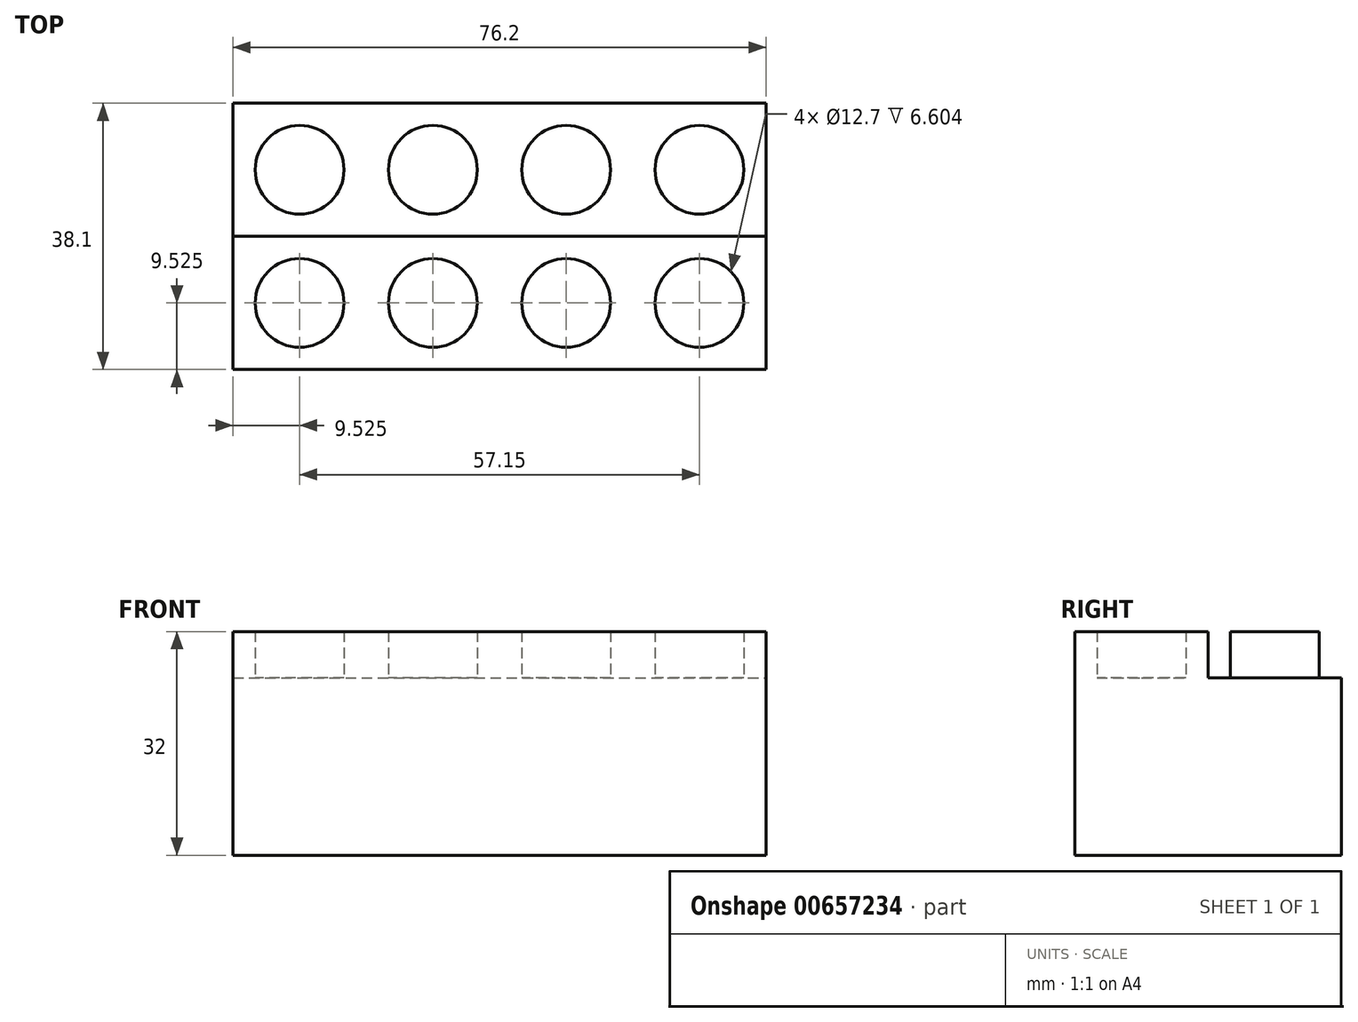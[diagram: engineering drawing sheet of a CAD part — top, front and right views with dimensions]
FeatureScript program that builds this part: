
annotation { "Feature Type Name" : "Feature", "Feature Type Description" : "" }
export const myFeature = defineFeature(function(context is Context, id is Id, definition is map)
    precondition{}
    {
        {
            var Q0;
            Q0=qCreatedBy(makeId("Top.planeOp"),FACE);
            var sketch = newSketch(context, id + "F0", { "sketchPlane" : qUnion([Q0])});
            skLineSegment(sketch, "E0.bottom", {"start": v(0, 0) * mm, "end": v(-76.2, 0) * mm});
            skLineSegment(sketch, "E0.top", {"start": v(0, 38.1) * mm, "end": v(-76.2, 38.1) * mm});
            skLineSegment(sketch, "E0.left", {"start": v(0, 0) * mm, "end": v(0, 38.1) * mm});
            skLineSegment(sketch, "E0.right", {"start": v(-76.2, 0) * mm, "end": v(-76.2, 38.1) * mm});
            skSolve(sketch);
        }
        {
            var Q0;
            Q0=makeQuery(id+"F0.imprint","IMPRINT",FACE,{"disambiguationData":[TD([[makeQuery(id+"F0.imprint","IMPRINT",EDGE,{"derivedFrom":sQuery(id+"F0.wireOp",EDGE,"E0.bottom")}),-1.0]])]});
            extrude(context, id + "F1", {"entities" : qUnion([Q0]), "depth" : 25.4 * mm, "offsetDistance" : 25.4 * mm});
        }
        {
            var Q0;
            Q0=makeQuery(id+"F1.opExtrude","CAP_FACE",FACE,{"disambiguationData":[OSD([sQuery(id+"F0.wireOp",EDGE,"E0.bottom"),sQuery(id+"F0.wireOp",EDGE,"E0.top"),sQuery(id+"F0.wireOp",EDGE,"E0.left"),sQuery(id+"F0.wireOp",EDGE,"E0.right")])],"isStart":false});
            var sketch = newSketch(context, id + "F2", { "sketchPlane" : qUnion([Q0])});
            skLineSegment(sketch, "E1", {"start": v(-76.2, 19.05) * mm, "end": v(0, 19.05) * mm});
            skLineSegment(sketch, "E2", {"start": v(-57.15, 38.1) * mm, "end": v(-57.15, 0) * mm});
            skLineSegment(sketch, "E3", {"start": v(-19.05, 38.1) * mm, "end": v(-19.05, 0) * mm});
            skLineSegment(sketch, "E4", {"start": v(-38.1, 38.1) * mm, "end": v(-38.1, 0) * mm});
            skLineSegment(sketch, "E5", {"start": v(-57.15, 19.05) * mm, "end": v(-57.15, 38.1) * mm});
            skCircle(sketch, "E6", {"center": v(-66.68, 28.57) * mm, "radius": 6.35 * mm});
            skCircle(sketch, "E7", {"center": v(-47.63, 28.57) * mm, "radius": 6.35 * mm});
            skCircle(sketch, "E8", {"center": v(-28.57, 28.57) * mm, "radius": 6.35 * mm});
            skCircle(sketch, "E9", {"center": v(-9.52, 28.57) * mm, "radius": 6.35 * mm});
            skCircle(sketch, "E10.MirrorC", {"center": v(-66.68, 9.53) * mm, "radius": 6.35 * mm});
            skCircle(sketch, "E11.MirrorC", {"center": v(-47.63, 9.52) * mm, "radius": 6.35 * mm});
            skCircle(sketch, "E12.MirrorC", {"center": v(-28.57, 9.52) * mm, "radius": 6.35 * mm});
            skCircle(sketch, "E13.MirrorC", {"center": v(-9.52, 9.52) * mm, "radius": 6.35 * mm});
            skSolve(sketch);
        }
        {
            var Q0;
            Q0=makeQuery(id+"F2.imprint","IMPRINT",FACE,{"disambiguationData":[TD([[makeQuery(id+"F2.imprint","IMPRINT",EDGE,{"derivedFrom":sQuery(id+"F2.wireOp",EDGE,"E6")}),1.0]])]});
            var Q1;
            Q1=makeQuery(id+"F2.imprint","IMPRINT",FACE,{"disambiguationData":[TD([[makeQuery(id+"F2.imprint","IMPRINT",EDGE,{"derivedFrom":sQuery(id+"F2.wireOp",EDGE,"E7")}),1.0]])]});
            var Q2;
            Q2=makeQuery(id+"F2.imprint","IMPRINT",FACE,{"disambiguationData":[TD([[makeQuery(id+"F2.imprint","IMPRINT",EDGE,{"derivedFrom":sQuery(id+"F2.wireOp",EDGE,"E8")}),1.0]])]});
            var Q3;
            Q3=makeQuery(id+"F2.imprint","IMPRINT",FACE,{"disambiguationData":[TD([[makeQuery(id+"F2.imprint","IMPRINT",EDGE,{"derivedFrom":sQuery(id+"F2.wireOp",EDGE,"E9")}),1.0]])]});
            var Q4;
            Q4=makeQuery(id+"F2.imprint","IMPRINT",FACE,{"disambiguationData":[TD([[makeQuery(id+"F2.imprint","IMPRINT",EDGE,{"derivedFrom":sQuery(id+"F2.wireOp",EDGE,"E13.MirrorC")}),-1.0]])]});
            var Q5;
            Q5=makeQuery(id+"F2.imprint","IMPRINT",FACE,{"disambiguationData":[TD([[makeQuery(id+"F2.imprint","IMPRINT",EDGE,{"derivedFrom":sQuery(id+"F2.wireOp",EDGE,"E12.MirrorC")}),-1.0]])]});
            var Q6;
            Q6=makeQuery(id+"F2.imprint","IMPRINT",FACE,{"disambiguationData":[TD([[makeQuery(id+"F2.imprint","IMPRINT",EDGE,{"derivedFrom":sQuery(id+"F2.wireOp",EDGE,"E11.MirrorC")}),-1.0]])]});
            var Q7;
            Q7=makeQuery(id+"F2.imprint","IMPRINT",FACE,{"disambiguationData":[TD([[makeQuery(id+"F2.imprint","IMPRINT",EDGE,{"derivedFrom":sQuery(id+"F2.wireOp",EDGE,"E10.MirrorC")}),-1.0]])]});
            extrude(context, id + "F3", {"entities" : qUnion([Q0, Q1, Q2, Q3, Q4, Q5, Q6, Q7]), "operationType" : NewBodyOperationType.ADD, "depth" : 6.6 * mm, "offsetDistance" : 25.4 * mm});
        }
    });
